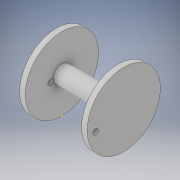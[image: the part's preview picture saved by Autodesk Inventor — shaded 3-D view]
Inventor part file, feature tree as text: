
AUTODESK INVENTOR PART (.ipt)
format: ipt  version: 2019 (Build 230136000, 136)  size: 120,320 bytes
history: native  units: in
note: dims shown in document units (in); Inventor stores cm internally (conversion verified against a paired STEP export)
features: sketch x6, hole x2, revolve x1
ambient origin geometry x8: Origin, YZ Plane, XZ Plane, XY Plane, X Axis, Y Axis, Z Axis, Center Point
bodies: Solid1 (feature_tree)
feature tree (9):
  revolve  "Revolution1"  [1 undecoded]
  hole  "Hole1"  [1 undecoded]
  hole  "Hole2"  [1 undecoded]
  sketch  "Sketch4"  dims[d6=0.0787in d7=0.2362in d8=0.1575in d9=0.0787in d10=90.0deg d11=0.315in d12=0.8108in]
  sketch  "Sketch5"  dims[d13=0.0787in d14=0.2362in d15=0.1575in d16=0.0787in d17=90.0deg d18=0.315in d19=0.8108in]
  sketch  "Sketch6"
  sketch  "Sketch1"  dims[d0=0.5118in d1=0.9449in]
  sketch  "Sketch2"  dims[d2=0.0787in d3=0.3937in]
  sketch  "Sketch3"  dims[d4=0.7874in d5=90.0deg]
note: 3 required parameter values undecoded (feature->parameter linkage not recoverable at this tier; creation-order binding heuristic only, values carry confidence <= 0.55)